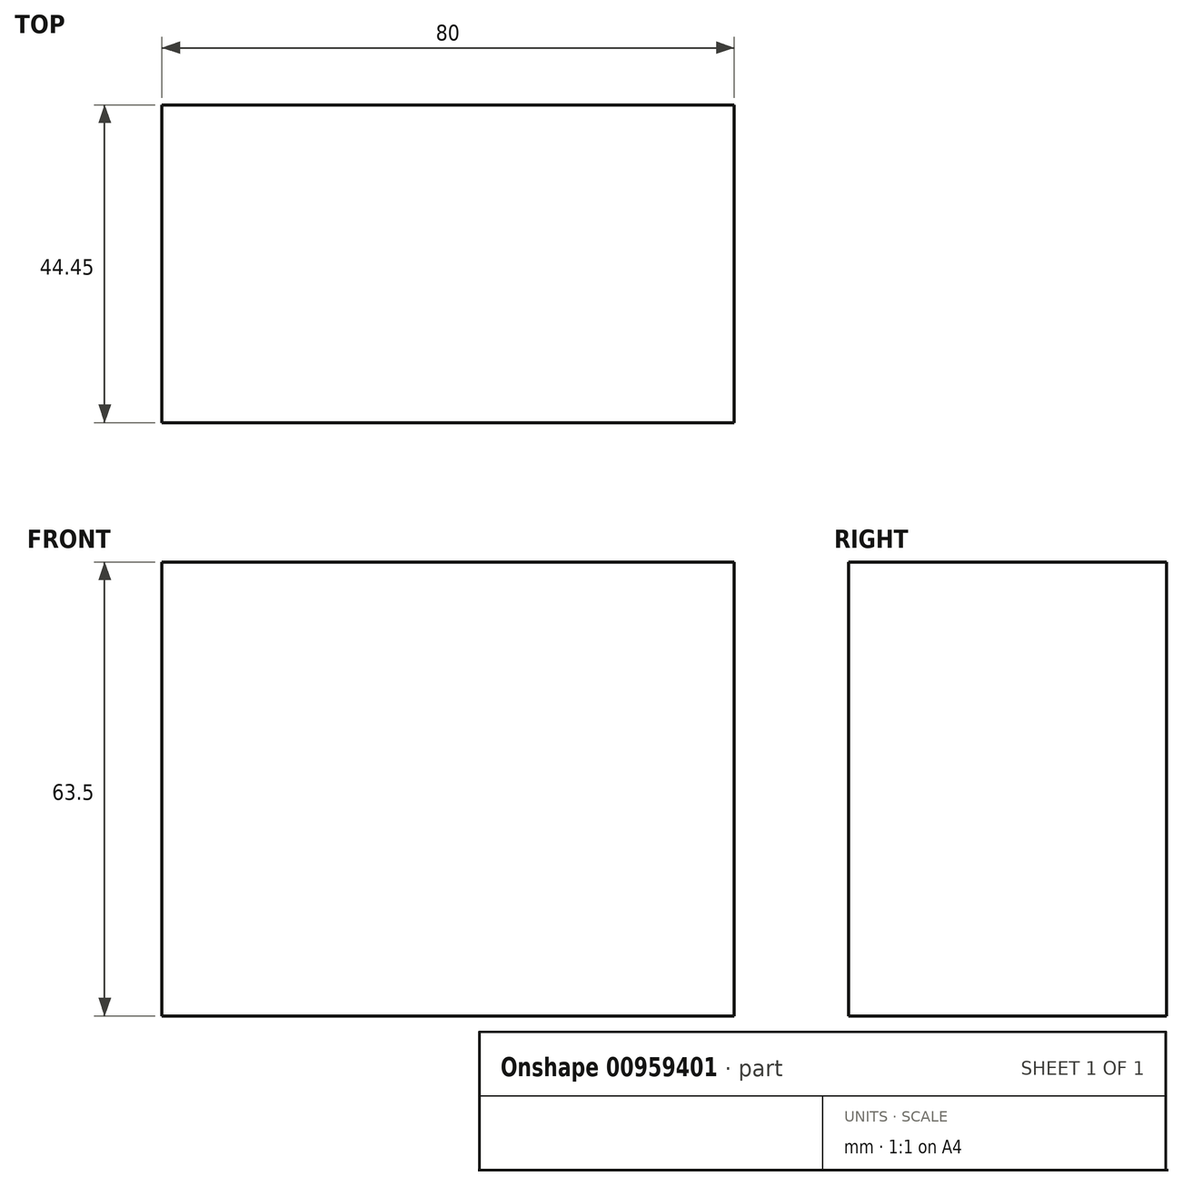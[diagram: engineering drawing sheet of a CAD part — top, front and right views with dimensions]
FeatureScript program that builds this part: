
annotation { "Feature Type Name" : "Feature", "Feature Type Description" : "" }
export const myFeature = defineFeature(function(context is Context, id is Id, definition is map)
    precondition{}
    {
        {
            assignVariable(context, id + "F0", {"name" : "width", "anyValue" : 80});
        }
        {
            var Q0;
            Q0=qCreatedBy(makeId("Right.planeOp"),FACE);
            var sketch = newSketch(context, id + "F1", { "sketchPlane" : qUnion([Q0])});
            skLineSegment(sketch, "E0.bottom", {"start": v(0, 0) * mm, "end": v(-44.45, 0) * mm});
            skLineSegment(sketch, "E0.top", {"start": v(0, 63.5) * mm, "end": v(-44.45, 63.5) * mm});
            skLineSegment(sketch, "E0.left", {"start": v(0, 0) * mm, "end": v(0, 63.5) * mm});
            skLineSegment(sketch, "E0.right", {"start": v(-44.45, 0) * mm, "end": v(-44.45, 63.5) * mm});
            skSolve(sketch);
        }
        {
            var Q0;
            Q0=makeQuery(id+"F1.imprint","IMPRINT",FACE,{"disambiguationData":[TD([[makeQuery(id+"F1.imprint","IMPRINT",EDGE,{"derivedFrom":sQuery(id+"F1.wireOp",EDGE,"E0.bottom")}),-1.0]])]});
            extrude(context, id + "F2", {"entities" : qUnion([Q0]), "depth" : (getVariable(context, 'width')) * mm, "offsetDistance" : 25.4 * mm});
        }
    });
